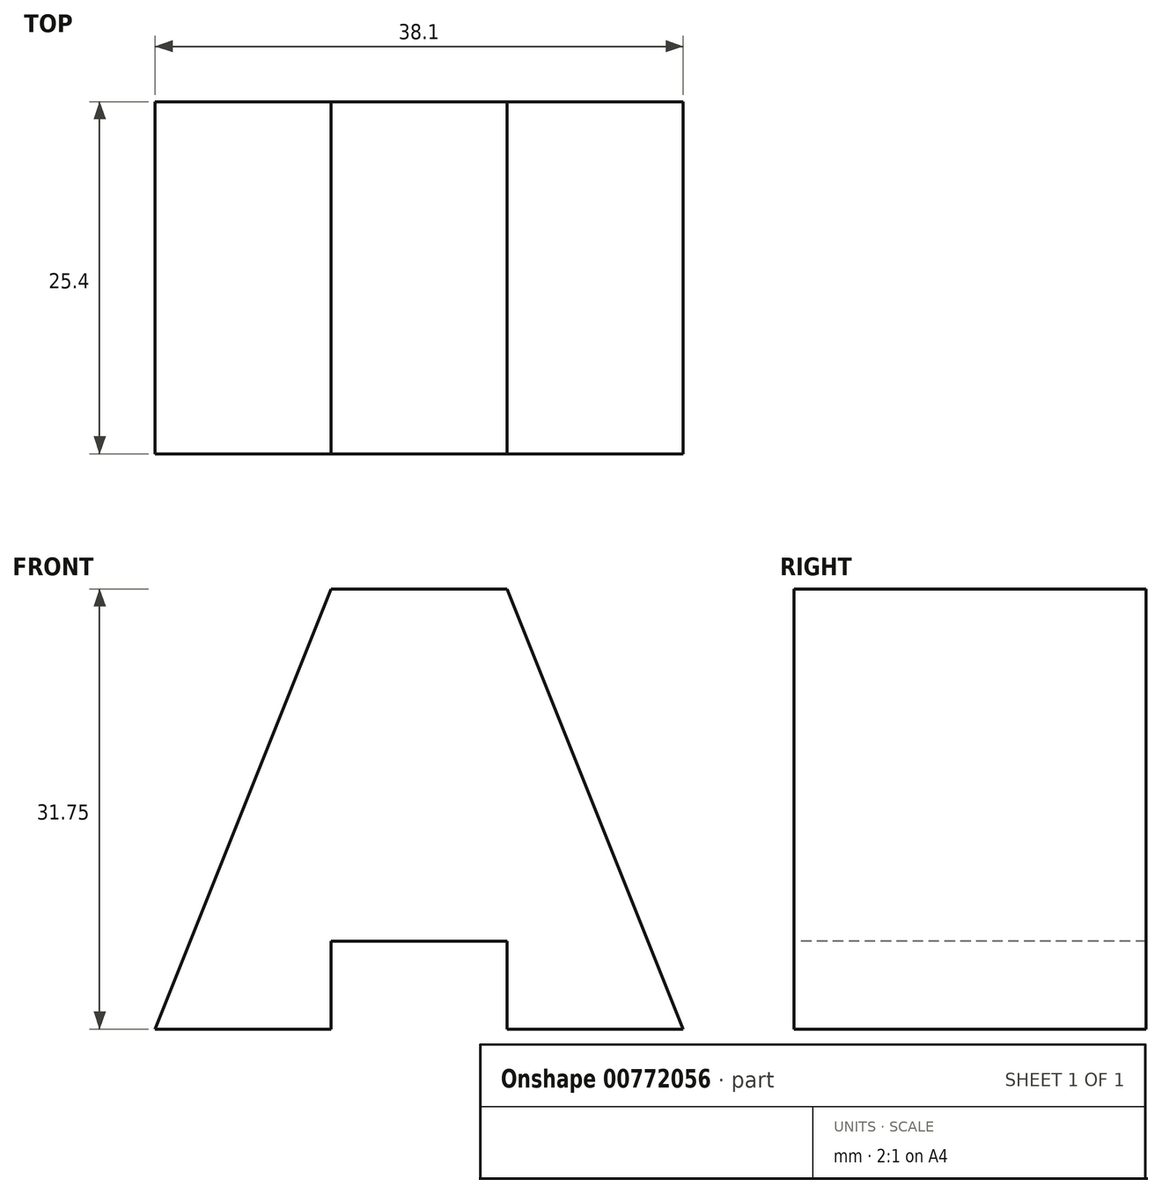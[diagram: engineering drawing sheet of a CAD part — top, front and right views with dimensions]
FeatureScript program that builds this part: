
annotation { "Feature Type Name" : "Feature", "Feature Type Description" : "" }
export const myFeature = defineFeature(function(context is Context, id is Id, definition is map)
    precondition{}
    {
        {
            var Q0;
            Q0=qCreatedBy(makeId("Front.planeOp"),FACE);
            var sketch = newSketch(context, id + "F0", { "sketchPlane" : qUnion([Q0])});
            skLineSegment(sketch, "E0", {"start": v(0, 0) * mm, "end": v(38.1, 0) * mm});
            skLineSegment(sketch, "E1", {"start": v(38.1, 0) * mm, "end": v(38.1, 31.75) * mm});
            skLineSegment(sketch, "E2", {"start": v(38.1, 31.75) * mm, "end": v(0, 31.75) * mm});
            skLineSegment(sketch, "E3", {"start": v(0, 31.75) * mm, "end": v(0, 0) * mm});
            skSolve(sketch);
        }
        {
            var Q0;
            Q0=makeQuery(id+"F0.imprint","IMPRINT",FACE,{"disambiguationData":[TD([[makeQuery(id+"F0.imprint","IMPRINT",EDGE,{"derivedFrom":sQuery(id+"F0.wireOp",EDGE,"E0")}),1.0]])]});
            extrude(context, id + "F1", {"entities" : qUnion([Q0]), "depth" : 25.4 * mm, "offsetDistance" : 25.4 * mm});
        }
        {
            var Q0;
            Q0=makeQuery(id+"F1.opExtrude","CAP_FACE",FACE,{"disambiguationData":[OSD([sQuery(id+"F0.wireOp",EDGE,"E0"),sQuery(id+"F0.wireOp",EDGE,"E1"),sQuery(id+"F0.wireOp",EDGE,"E2"),sQuery(id+"F0.wireOp",EDGE,"E3")])],"isStart":false});
            var sketch = newSketch(context, id + "F2", { "sketchPlane" : qUnion([Q0])});
            skLineSegment(sketch, "E4", {"start": v(0, 31.75) * mm, "end": v(12.7, 31.75) * mm});
            skLineSegment(sketch, "E5", {"start": v(12.7, 31.75) * mm, "end": v(0, 0) * mm});
            skLineSegment(sketch, "E6", {"start": v(38.1, 31.75) * mm, "end": v(25.4, 31.75) * mm});
            skLineSegment(sketch, "E7", {"start": v(25.4, 31.75) * mm, "end": v(38.1, 0) * mm});
            skSolve(sketch);
        }
        {
            var Q0;
            Q0=makeQuery(id+"F2.imprint","IMPRINT",FACE,{"disambiguationData":[TD([[makeQuery(id+"F2.imprint","IMPRINT",EDGE,{"derivedFrom":sQuery(id+"F2.wireOp",EDGE,"E4")}),1.0]])]});
            var sketch = newSketch(context, id + "F3", { "sketchPlane" : qUnion([Q0])});
            skSolve(sketch);
        }
        {
            var Q0;
            Q0=makeQuery(id+"F3.imprint","IMPRINT",FACE,{"disambiguationData":[TD([[makeQuery(id+"F3.imprint","IMPRINT",EDGE,{"derivedFrom":makeQuery(id+"F2.imprint","IMPRINT",EDGE,{"derivedFrom":sQuery(id+"F2.wireOp",EDGE,"E4")})}),1.0]])]});
            extrude(context, id + "F4", {"entities" : qUnion([Q0]), "operationType" : NewBodyOperationType.REMOVE, "oppositeDirection" : true, "depth" : 25.4 * mm, "offsetDistance" : 25.4 * mm});
        }
        {
            var Q0;
            Q0=makeQuery(id+"F2.imprint","IMPRINT",FACE,{"disambiguationData":[TD([[makeQuery(id+"F2.imprint","IMPRINT",EDGE,{"derivedFrom":sQuery(id+"F2.wireOp",EDGE,"E6")}),1.0]])]});
            extrude(context, id + "F5", {"entities" : qUnion([Q0]), "operationType" : NewBodyOperationType.REMOVE, "oppositeDirection" : true, "depth" : 25.4 * mm, "offsetDistance" : 25.4 * mm});
        }
        {
            var Q0;
            Q0=makeQuery(id+"F1.opExtrude","CAP_FACE",FACE,{"disambiguationData":[OSD([sQuery(id+"F0.wireOp",EDGE,"E0"),sQuery(id+"F0.wireOp",EDGE,"E1"),sQuery(id+"F0.wireOp",EDGE,"E2"),sQuery(id+"F0.wireOp",EDGE,"E3")])],"isStart":false});
            var sketch = newSketch(context, id + "F6", { "sketchPlane" : qUnion([Q0])});
            skLineSegment(sketch, "E8", {"start": v(12.7, 0) * mm, "end": v(12.7, 6.35) * mm});
            skLineSegment(sketch, "E9", {"start": v(12.7, 6.35) * mm, "end": v(25.4, 6.35) * mm});
            skLineSegment(sketch, "E10", {"start": v(25.4, 6.35) * mm, "end": v(25.4, 0) * mm});
            skSolve(sketch);
        }
        {
            var Q0;
            {var subQ0=sQuery(id+"F6.wireOp",EDGE,"E8");Q0=makeQuery(id+"F6.imprint","IMPRINT",FACE,{"disambiguationData":[TD([[makeQuery(id+"F6.imprint","IMPRINT",EDGE,{"derivedFrom":subQ0}),-1.0]])]});}
            extrude(context, id + "F7", {"entities" : qUnion([Q0]), "operationType" : NewBodyOperationType.REMOVE, "oppositeDirection" : true, "depth" : 25.4 * mm, "offsetDistance" : 25.4 * mm});
        }
    });
